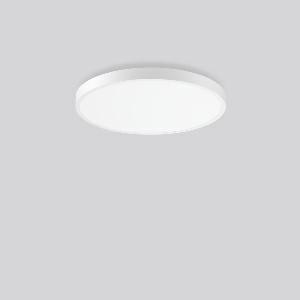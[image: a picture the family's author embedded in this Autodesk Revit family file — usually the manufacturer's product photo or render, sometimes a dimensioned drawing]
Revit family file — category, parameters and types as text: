
# Revit family: triona_round_a_312387_002_2_76_51e9
name_source: partatom
category: Lighting Fixtures
units: mm (PartAtom-declared; Revit-internal decimal feet)

## family parameters
Cut with Voids When Loaded = No
Host = Face
Light Source = No
Part Type = Normal
Room Calculation Point = No
Round Connector Dimension = Use Diameter
Shared = No

## types (1)
- TuneableWhite 846 (1 x LED Modul 846, 4800 lm, 4600)
    Apparent Load = 49 VA
    CIE Flux Codes = 50 80 96 100 100
    Color Rendering = 80
    Color Temperature = 4600
    Default Elevation = 1800 mm
    Description = Series: TRIONA round
Decorative round LED surface-mounted luminaire. Flat, seamless frame: aluminium extrusion profile, powder coated. Cover made of sheet steel, powder-coated. Light emission through a diffuser: plastic, opal. Lightguide and diffuser made of non-yellowing plastic (PMMA). Lateral light emission (RZB SIDELITE technology) for above-average homogeneous light distribution. Tunable white versions, dynamically adjustable from 2700 K to 6500 K. Suitable for Ceiling mounting, Wall (surface). Tool-free mounting via bayonet connection. Electronic ballast included. Very easy installation thanks to Plug+Play connection. Ideal for use as part of the Human Centric Lighting concept in connection with RZB light management systems. 
Colour: traffic white, matt (RAL 9016)
Diameter: 845 mm
Height: 88 mm
Lamp: LED
Socket: without socket
Colour temperature: 2700K - 6500K
Colour rendering index (CRI): 80
System power: 49 W
Rated luminous flux: 4800 lm
Luminous efficiency: 98 lm/W
System power 2: 51 W
Rated luminous flux 2: 4550 lm
Luminous efficiency 2: 89 lm/W
System power 3: 51 W
Rated luminous flux 3: 4650 lm
Luminous efficiency 3: 91 lm/W
Control gear: Converter, dimmable, DALI
Protection class: I
Type of protection: IP 20
    Height = 88 mm
    Lamp = 1 x LED Modul 846
    Lamp Light Flux = 4800 lm
    Lamp count = 1
    Length = 845 mm
    Lifetime = 50000 h
    Luminous efficacy = 98 lm/W
    Manufacturer = RZB
    ModVariant = No
    Model = 312387.002.2.76
    Mounting Place = Ceiling
    Mounting Type = Surface mounted
    Number of Poles = 1
    OnlyDefault = Yes
    Power Factor = 1
    Product Name = TRIONA round A
    Product group = Surface mounted modular luminaires
    ProductGroupID = 306
    Protection Class = Protection class I
    Protection Degree = IP 20
    RLX_Detail_Level = 1
    RLX_Emergency_Light_Flux = 0 lm
    RLX_Emergency_Type = 0
    RLX_Emergency_Type_DB = No
    RlxData = <blob elided: 31029 chars, md5=8f52ca10>
    Socket = socket
    Standby Power = 0 W
    System Light Flux = 4800 lm
    System Power = 49 W
    Type Comments = TuneableWhite 846
    Type Image = 312384.002.jpg
    URL = http://relux.com
    VarID = tuneablewhite_846
    Voltage = 230 V
    Voltage Range = 220-240 V
    Weight = 0.00 kg
    Width = 0 mm  [stored 0 ft]

note: [stored X ft] marks values corroborated as IEEE doubles in the binary element streams (Revit-internal decimal feet)

## geometry (parser evidence)
native form markers: Blend x4, Sweep x10
no freeform markers — native parametric forms only
